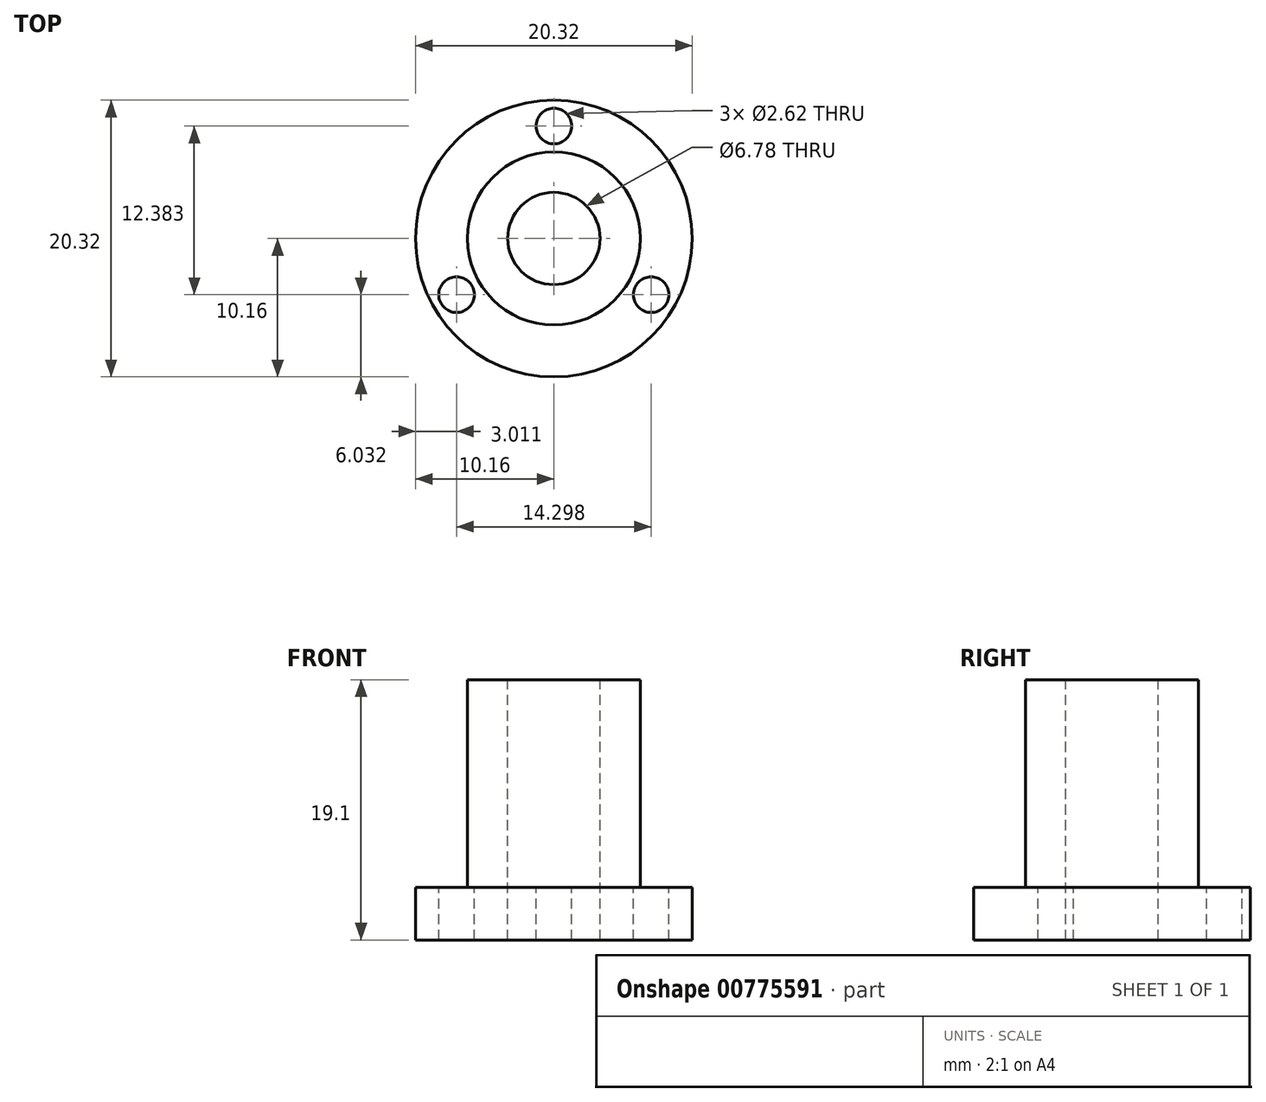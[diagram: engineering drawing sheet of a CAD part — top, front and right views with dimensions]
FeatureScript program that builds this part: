
annotation { "Feature Type Name" : "Feature", "Feature Type Description" : "" }
export const myFeature = defineFeature(function(context is Context, id is Id, definition is map)
    precondition{}
    {
        {
            var Q0;
            Q0=qCreatedBy(makeId("Top.planeOp"),FACE);
            var sketch = newSketch(context, id + "F0", { "sketchPlane" : qUnion([Q0])});
            skCircle(sketch, "E0", {"center": v(0, 0) * mm, "radius": 10.16 * mm});
            skSolve(sketch);
        }
        {
            var Q0;
            Q0 = qSketchRegion(id + "F0", true);
            extrude(context, id + "F1", {"entities" : qUnion([Q0]), "depth" : 3.86 * mm, "offsetDistance" : 25.4 * mm});
        }
        {
            var Q0;
            Q0=makeQuery(id+"F1.opExtrude","CAP_FACE",FACE,{"disambiguationData":[OSD([sQuery(id+"F0.wireOp",EDGE,"E0")])],"isStart":false});
            var sketch = newSketch(context, id + "F2", { "sketchPlane" : qUnion([Q0])});
            skCircle(sketch, "E1", {"center": v(0, 0) * mm, "radius": 6.35 * mm});
            skSolve(sketch);
        }
        {
            var Q0;
            Q0 = qSketchRegion(id + "F2", true);
            extrude(context, id + "F3", {"entities" : qUnion([Q0]), "operationType" : NewBodyOperationType.ADD, "depth" : 15.24 * mm, "offsetDistance" : 25.4 * mm});
        }
        {
            var Q0;
            Q0=makeQuery(id+"F1.opExtrude","CAP_FACE",FACE,{"disambiguationData":[OSD([sQuery(id+"F0.wireOp",EDGE,"E0")])],"isStart":false});
            var sketch = newSketch(context, id + "F4", { "sketchPlane" : qUnion([Q0])});
            skCircle(sketch, "E2", {"center": v(0, 8.26) * mm, "radius": 1.3 * mm});
            skLineSegment(sketch, "E3", {"start": v(0, 10.16) * mm, "end": v(0, 6.35) * mm});
            skCircle(sketch, "E4.1.0", {"center": v(-7.15, -4.13) * mm, "radius": 1.3 * mm});
            skCircle(sketch, "E4.2.0", {"center": v(7.15, -4.13) * mm, "radius": 1.3 * mm});
            skPoint(sketch, "E4.center", {"position": v(0, 0) * mm});
            skSolve(sketch);
        }
        {
            var Q0;
            Q0 = qSketchRegion(id + "F4", true);
            extrude(context, id + "F5", {"entities" : qUnion([Q0]), "operationType" : NewBodyOperationType.REMOVE, "endBound" : BoundingType.UP_TO_NEXT, "oppositeDirection" : true, "depth" : 25.4 * mm, "offsetDistance" : 25.4 * mm});
        }
        {
            var Q0;
            Q0=makeQuery(id+"F3.opExtrude","CAP_FACE",FACE,{"disambiguationData":[OSD([sQuery(id+"F2.wireOp",EDGE,"E1")])],"isStart":false});
            var sketch = newSketch(context, id + "F6", { "sketchPlane" : qUnion([Q0])});
            skCircle(sketch, "E5", {"center": v(0, 0) * mm, "radius": 3.4 * mm});
            skSolve(sketch);
        }
        {
            var Q0;
            Q0 = qSketchRegion(id + "F6", true);
            extrude(context, id + "F7", {"entities" : qUnion([Q0]), "operationType" : NewBodyOperationType.REMOVE, "endBound" : BoundingType.UP_TO_NEXT, "oppositeDirection" : true, "depth" : 25.4 * mm, "offsetDistance" : 25.4 * mm});
        }
    });
